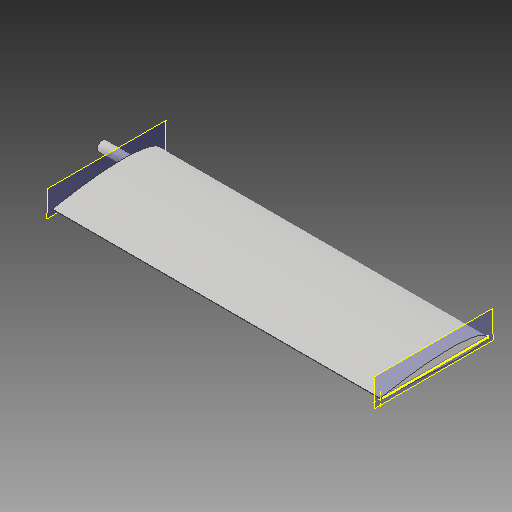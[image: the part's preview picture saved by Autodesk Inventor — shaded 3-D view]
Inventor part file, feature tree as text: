
AUTODESK INVENTOR PART (.ipt)
format: ipt  version: 2018 (Build 220112000, 112)  size: 106,496 bytes
history: native  units: in
note: dims shown in document units (in); Inventor stores cm internally (conversion verified against a paired STEP export)
features: other x3, sketch x3, plane x3
ambient origin geometry x8: Origin, YZ Plane, XZ Plane, XY Plane, X Axis, Y Axis, Z Axis, Center Point
bodies: Solid1 (feature_tree)
feature tree (9):
  other  "Generic Wing 1.ipt"
  other  "Solid1::Generic Wing 1.ipt"
  other  "TaggingFeature1"
  sketch  "Sketch1"  dims[d0=0.3937in]
  sketch  "Sketch2"
  sketch  "Sketch3"
  plane  "Work Plane1"
  plane  "Work Plane2"
  plane  "Work Plane3"
